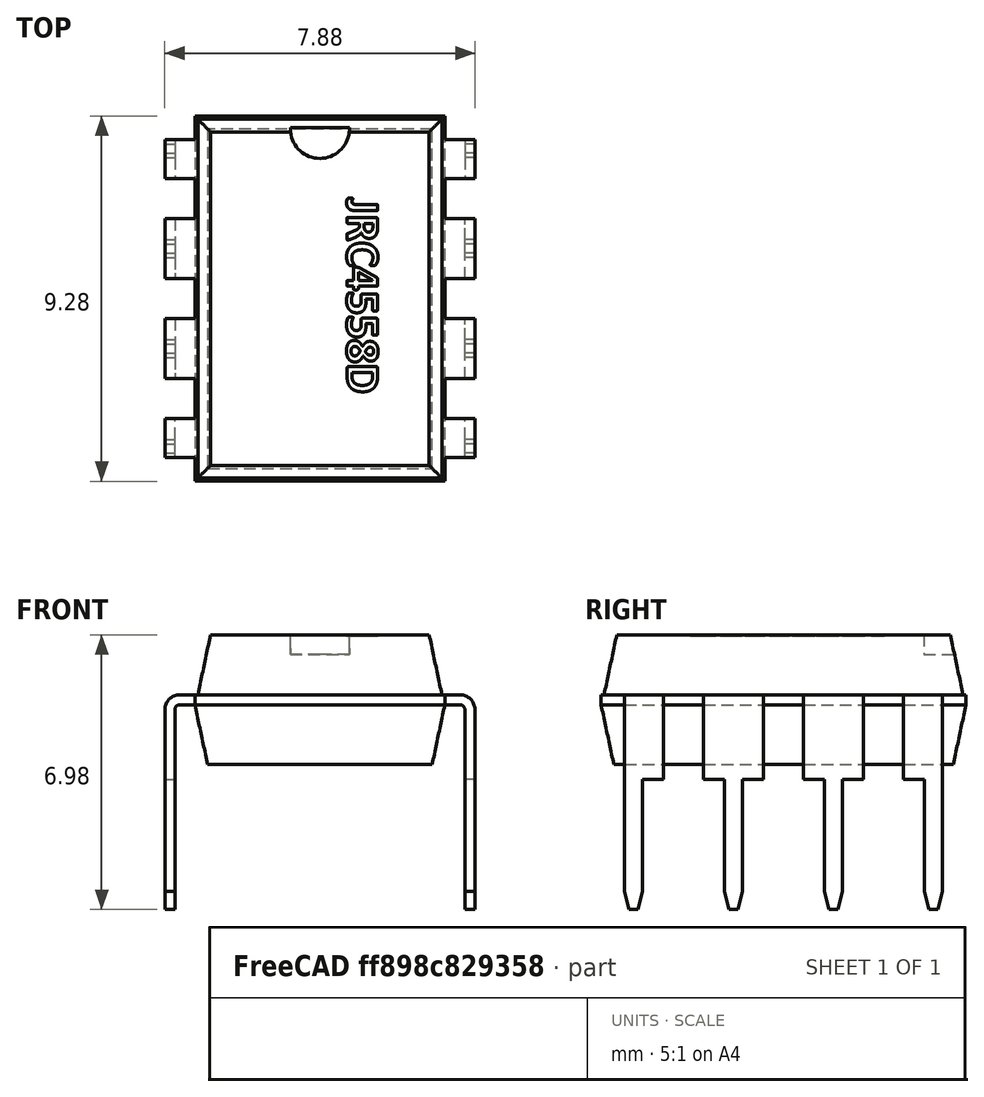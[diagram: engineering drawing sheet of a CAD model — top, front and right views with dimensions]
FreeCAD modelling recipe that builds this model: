
FCSTD DOCUMENT  (FreeCAD 0.17R13528 (Git))
Label: NiceTemplate
License: All rights reserved
LicenseURL: http://en.wikipedia.org/wiki/All_rights_reserved
objects: Part::Cut×2, Part::Feature×1, Part::Part2DObjectPython×1, Part::Extrusion×1
note: 5 computed .brp shape members not serialized (recipe doc carries the construction recipe); baked Part::Feature solids carry a one-line shape summary decoded from their .brp

FEATURE [Part::Feature] Part__Feature  label="DIP-8_W7.62mm"
  shape: bbox 7.874 x 9.27 x 6.98 mm, 148 faces (baked)
FEATURE [Part::Part2DObjectPython] ShapeString  # Draft 2D object (typed FeaturePython)
  FontFile = <userpath>/Desktop/Freecad Projects/calibrib.ttf
  Placement = pos=(4.5,-1.25,3.68) rot=(0,0,1;-1.5708rad)
  Size = 1
  String = JRC4558D
  Support = -> [Part__Feature]
  Tracking = 0
FEATURE [Part::Extrusion] Extrude
  Base = -> ShapeString
  Dir = (0,0,1)
  DirMode = 2
  FaceMakerClass = Part::FaceMakerBullseye
  LengthFwd = -0.025
  LengthRev = 0
  Solid = true
  Symmetric = false
FEATURE [Part::Cut] Cut
  Base = -> Part__Feature
  Tool = -> Extrude
FEATURE [Part::Cut] Cut001
  Base = -> Part__Feature
  Tool = -> Extrude
